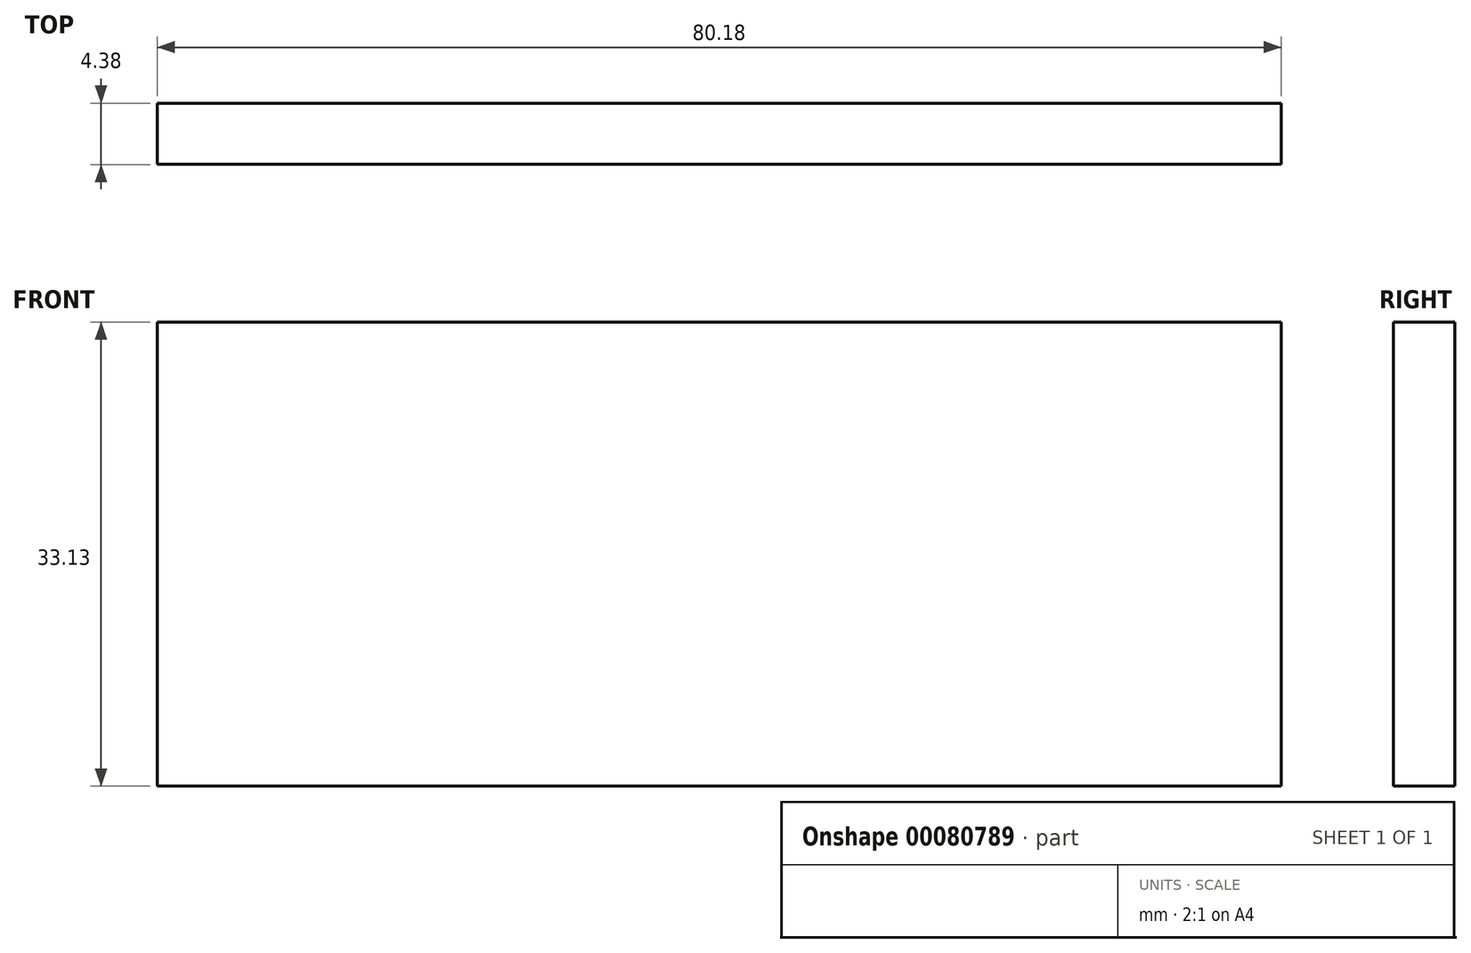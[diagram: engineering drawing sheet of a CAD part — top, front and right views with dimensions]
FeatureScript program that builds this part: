
annotation { "Feature Type Name" : "Feature", "Feature Type Description" : "" }
export const myFeature = defineFeature(function(context is Context, id is Id, definition is map)
    precondition{}
    {
        {
            var Q0;
            Q0=qCreatedBy(makeId("Front.planeOp"),FACE);
            var sketch = newSketch(context, id + "F0", { "sketchPlane" : qUnion([Q0])});
            skLineSegment(sketch, "E0.bottom", {"start": v(-33.53, 27.56) * mm, "end": v(46.65, 27.56) * mm});
            skLineSegment(sketch, "E0.top", {"start": v(-33.53, -5.57) * mm, "end": v(46.65, -5.57) * mm});
            skLineSegment(sketch, "E0.left", {"start": v(-33.53, 27.56) * mm, "end": v(-33.53, -5.57) * mm});
            skLineSegment(sketch, "E0.right", {"start": v(46.65, 27.56) * mm, "end": v(46.65, -5.57) * mm});
            skSolve(sketch);
        }
        {
            var Q0;
            Q0=makeQuery(id+"F0.imprint","IMPRINT",FACE,{"disambiguationData":[TD([[makeQuery(id+"F0.imprint","IMPRINT",EDGE,{"derivedFrom":sQuery(id+"F0.wireOp",EDGE,"E0.bottom")}),-1.0]])]});
            extrude(context, id + "F1", {"entities" : qUnion([Q0]), "depth" : 4.38 * mm});
        }
    });
